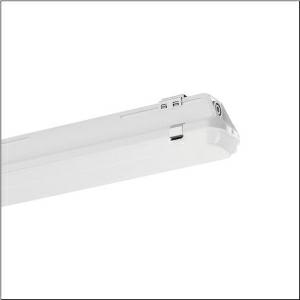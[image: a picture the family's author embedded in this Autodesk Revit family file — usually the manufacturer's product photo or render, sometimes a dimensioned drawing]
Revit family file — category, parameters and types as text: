
# Revit family: monsun_r__12_51fp20fp460h_3d07
name_source: partatom
category: Lighting Fixtures
units: mm (PartAtom-declared; Revit-internal decimal feet)

## family parameters
Cut with Voids When Loaded = No
Host = Face
Light Source = No
Part Type = Normal
Room Calculation Point = No
Round Connector Dimension = Use Diameter
Shared = No

## types (1)
- --- (1 x LED, 5450 lm, 34.6 W, 4000K)
    Apparent Load = 35 VA
    CIE Flux Codes = 45 75 93 94 100
    Color Rendering = 80
    Color Temperature = 4000K
    Default Elevation = 1800 mm
    Description = Monsun® 12, damp-proof luminaire, chain hanger, primary optical cover: enclosure, of PC, light emission: direct distribution, primary light characteristic: symmetric, installation type: suspended mounting, surface-mounted, horizontal mounting, vertical mounting, LED, rated luminous flux: 5.450lm, luminous efficacy: 158lm/W, light colour: 840, colour temperature: 4000K, control gear: ECG DALI, with terminal, 5-pole, max. 2.5mm², mains connection: 220..240V, AC, 50/60Hz, start of lifetime: 35W, end of lifetime: 39W, luminaire housing, of glass-fibre reinforced polyester, uncoated, bright grey, length: 1.590mm, width: 90mm, height: 88mm, clip for enclosure, of stainless steel (V2A), ceiling mounting element, of stainless steel (V2A), chain hanger, of stainless steel (V2A), protection rating (complete): IP66, insulation class (complete): insulation class I (protective earthing), certification: CE, ENEC, VDE, protection symbol: D, impact resistance: IK08, permissible operating ambient temperature: -25..+40°C, standard: EN 50419, EN 60598-2-1, no direct snow, no direct sun, no direct rain, for indoor or canopied outdoor use, corresponds to IFS (International Featured Standards) requirements for safety and quality in the food industry, packaging unit: 1 piece
    Height = 89 mm
    Lamp = 1 x LED
    Lamp Light Flux = 5450 lm
    Lamp Power = 34.6 W
    Lamp count = 1
    Length = 1590 mm
    Luminous efficacy = 158 lm/W
    Manufacturer = Siteco
    ModVariant = No
    Model = 51FP20FP460H
    Mounting Place = Ceiling
    Mounting Type = Pendant
    Number of Poles = 1
    OnlyDefault = Yes
    Power Factor = 1
    Product Name = Monsun® 12
    Product group = damp-proof luminaire | ceiling pendant
    ProductGroupID = 908
    Protection Class = Protection class I
    Protection Degree = IP 66
    RLX_Detail_Level = 1
    RlxData = <blob elided: 91585 chars, md5=97798b8d>
    Socket = socket
    Standby Power = 0 W
    System Light Flux = 5450 lm
    System Power = 35 W
    Type Comments = factory setting: luminous flux: 100 % | dim-lin: 254 | 232 mA
    Type Image = l_1004748.jpg
    URL = http://relux.com
    VarID = @adj_133777
    Voltage = 0 V
    Weight = 0.00 kg
    Width = 90 mm

## geometry (parser evidence)
native form markers: Blend x4, Sweep x12
no freeform markers — native parametric forms only
